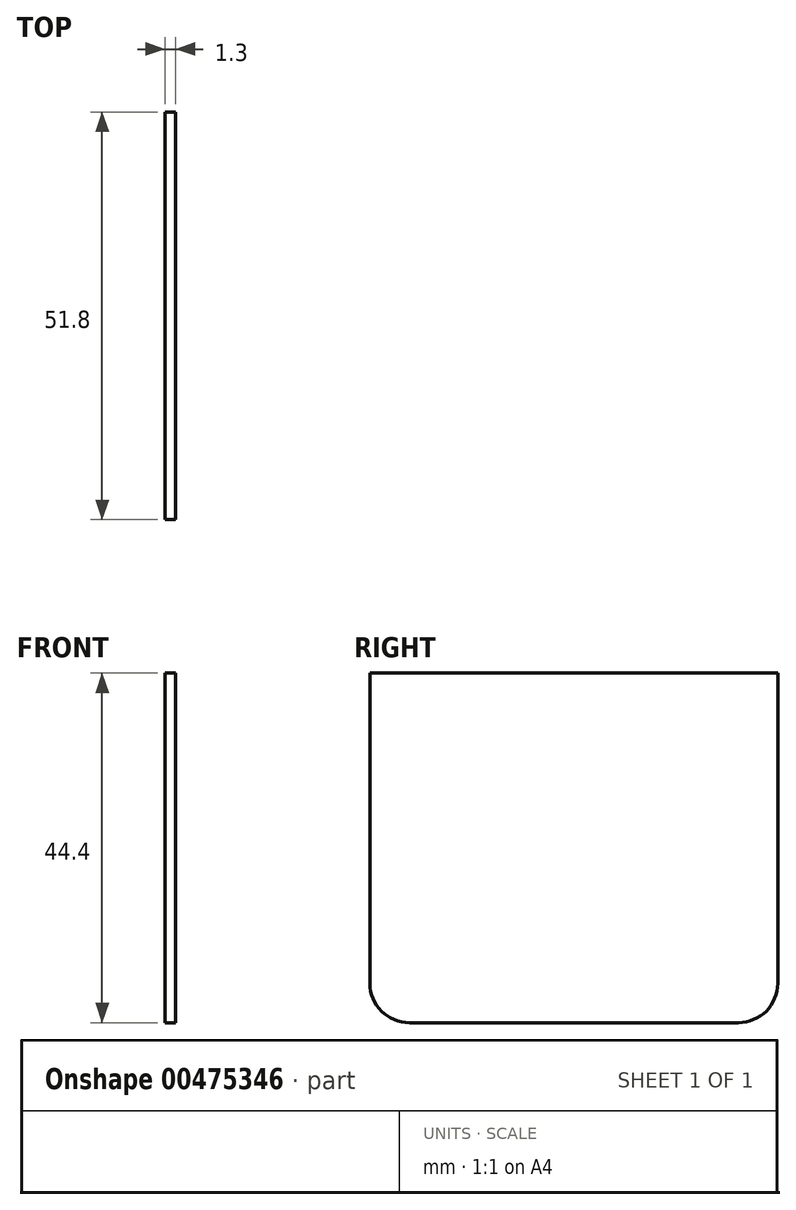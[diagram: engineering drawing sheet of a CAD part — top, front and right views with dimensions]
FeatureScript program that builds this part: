
annotation { "Feature Type Name" : "Feature", "Feature Type Description" : "" }
export const myFeature = defineFeature(function(context is Context, id is Id, definition is map)
    precondition{}
    {
        {
            var Q0;
            Q0=qCreatedBy(makeId("Right.planeOp"),FACE);
            var sketch = newSketch(context, id + "F0", { "sketchPlane" : qUnion([Q0])});
            skLineSegment(sketch, "E0.bottom", {"start": v(0, 0) * mm, "end": v(-51.8, 0) * mm});
            skLineSegment(sketch, "E0.top", {"start": v(0, 44.4) * mm, "end": v(-51.8, 44.4) * mm});
            skLineSegment(sketch, "E0.left", {"start": v(0, 0) * mm, "end": v(0, 44.4) * mm});
            skLineSegment(sketch, "E0.right", {"start": v(-51.8, 0) * mm, "end": v(-51.8, 44.4) * mm});
            skSolve(sketch);
        }
        {
            var Q0;
            Q0=makeQuery(id+"F0.imprint","IMPRINT",FACE,{"disambiguationData":[TD([[makeQuery(id+"F0.imprint","IMPRINT",EDGE,{"derivedFrom":sQuery(id+"F0.wireOp",EDGE,"E0.bottom")}),-1.0]])]});
            extrude(context, id + "F1", {"entities" : qUnion([Q0]), "depth" : 1.3 * mm, "offsetDistance" : 25 * mm});
        }
        {
            var Q0;
            Q0=makeQuery(id+"F1.opExtrude","SWEPT_EDGE",EDGE,{"disambiguationData":[OSD([sQuery(id+"F0.wireOp",EDGE,"E0.bottom"),sQuery(id+"F0.wireOp",EDGE,"E0.right")])]});
            var Q1;
            Q1=makeQuery(id+"F1.opExtrude","SWEPT_EDGE",EDGE,{"disambiguationData":[OSD([sQuery(id+"F0.wireOp",EDGE,"E0.bottom"),sQuery(id+"F0.wireOp",EDGE,"E0.left")])]});
            fillet(context, id + "F2", {"entities" : qUnion([Q0, Q1]), "tangentPropagation" : true, "radius" : 5 * mm, "defaultsChanged" : false, "vertexSettings" : [], "allowEdgeOverflow" : false});
        }
    });
